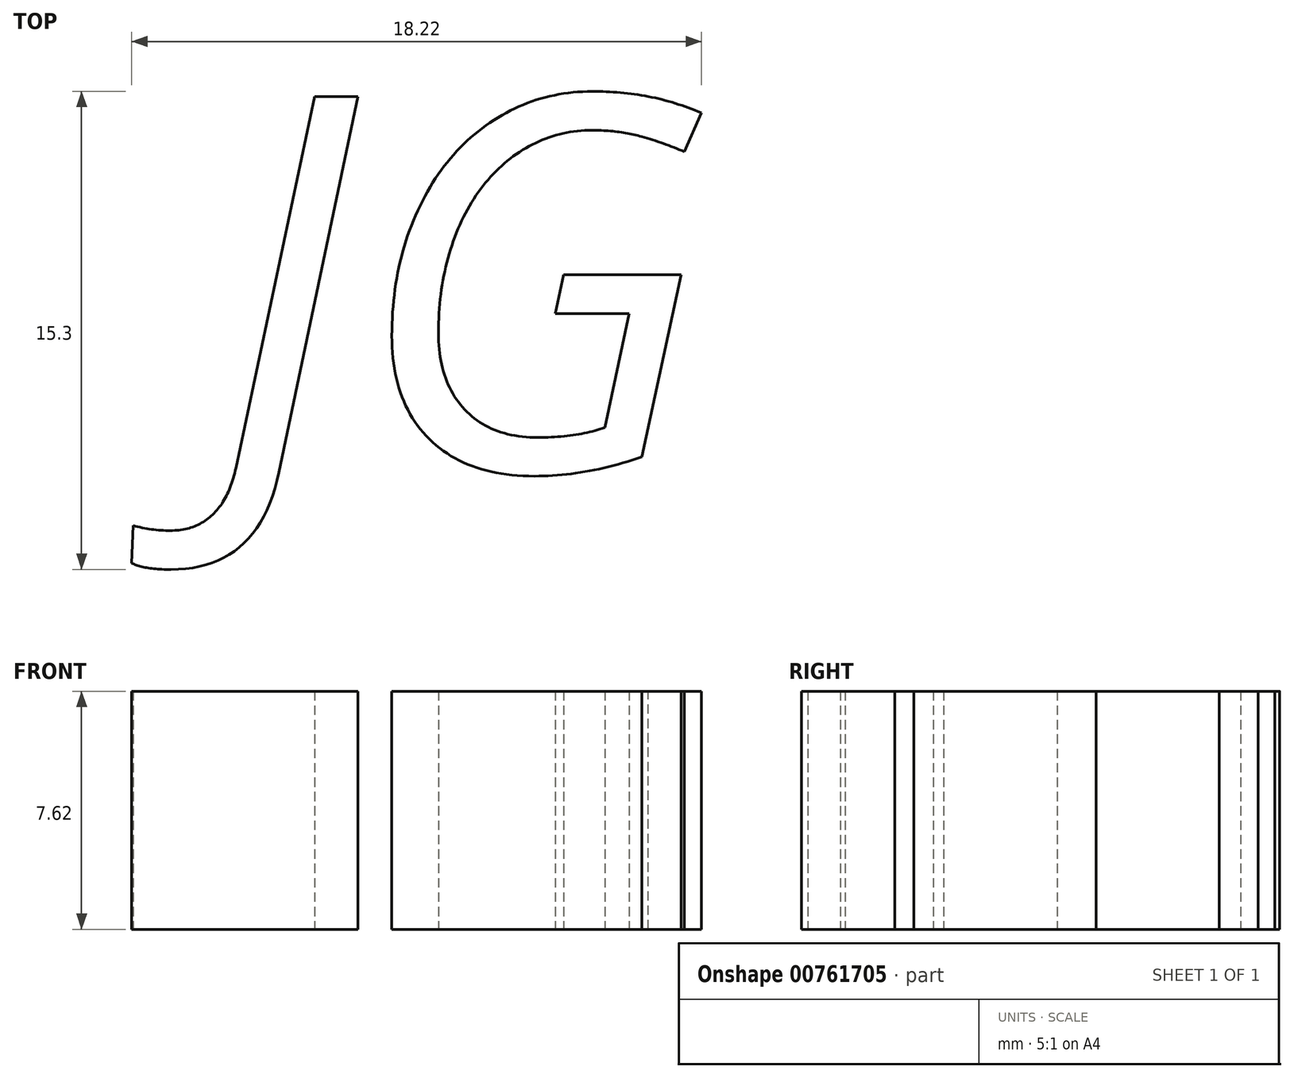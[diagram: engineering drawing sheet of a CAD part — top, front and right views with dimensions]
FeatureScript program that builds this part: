
annotation { "Feature Type Name" : "Feature", "Feature Type Description" : "" }
export const myFeature = defineFeature(function(context is Context, id is Id, definition is map)
    precondition{}
    {
        {
            var Q0;
            Q0=qCreatedBy(makeId("Top.planeOp"),FACE);
            var sketch = newSketch(context, id + "F0", { "sketchPlane" : qUnion([Q0])});
            skText(sketch, "E0", { "text": "JG", "fontName": "OpenSans-Italic.ttf"});
            const initialGuessF0  = {"E0": [-0.01705, 0.01034, 1, 0, 0.01208]};
            skSetInitialGuess(sketch, initialGuessF0);
            skSolve(sketch);
        }
        {
            var Q0;
            Q0 = qSketchRegion(id + "F0", true);
            extrude(context, id + "F1", {"entities" : qUnion([Q0]), "depth" : 7.62 * mm, "offsetDistance" : 25.4 * mm});
        }
    });
